# Revit family: Haworth_Planes_HeightAdjustTable_Corner90_WrapAround
name_source: partatom
category: Furniture Systems
revit_build: Autodesk Revit 2018 (Build: 20170223_1515(x64)
units: mm (PartAtom-declared; Revit-internal decimal feet)

## family parameters
Always vertical = Yes
Cut with Voids When Loaded = No
OmniClass Number = 23.40.70.14.64.21
OmniClass Title = Systems Furniture
Part Type = Normal
Room Calculation Point = No
Round Connector Dimension = Use Diameter
Shared = No
Work Plane-Based = No

## types (4) — shared parameters
Actual Height = 40"
Assembly Code = E2020200
Base Tube Finish = Haworth _ Paint _ Smoke
Custom Size = No
Edgeband = Yes
Height = 40"
Knife Edge = No
Leg Inset Length = 6"
Manufacturer = Haworth
Max. Depth = 29"
Max. Height = 46"
Max. Length = 70"
Max. Width = 70"
Min. Depth = 23"
Min. Height = 27"
Min. Length = 46"
Min. Width = 40"
Min/Max Depth = 23 or 29 in.
Min/Max Length = 46-70 in. @ 6 in. increment
Min/Max Width = 40-70 in. @ 6 in. increment
Model = TACR, TACE
Radius = 10 1/4"
Revision Number = 2
Size = Verify Final Dim. w/ Haworth
Support Height = 38 13/16"
Top Thickness = 1 3/16"
URL = www.haworth.com

## per-type parameters (varying)
| type | 23 Deep | Actual Depth | Actual Length | Actual Width | Back Leg Offset | Depth | Description | Length | URL - Product | Warranty | Width |
| 70" x 70" x 29" | No | 29" | 70" | 70" | 9 3/32" | 29" | Haworth Planes - HAT Corner-90 - WrapAround - 70" x 70" x 29" | 70" | https://www.haworth.com | https://www.haworth.com | 70" |
| 52" x 52" x 23" | Yes | 23" | 52" | 52" | 6 3/32" | 23" | Haworth Planes - HAT Corner-90 - WrapAround - 52" x 52" x 23" | 52" | http://www.haworth.com | www.haworth.com/en-us/Products/Pages/Certifications.aspx | 52" |
| 46" x 58" x 23" | Yes | 23" | 58" | 46" | 6 3/32" | 23" | Haworth Planes - HAT Corner-90 - WrapAround - 46" x 58" x 23" | 58" | http://www.haworth.com | www.haworth.com/en-us/Products/Pages/Certifications.aspx | 46" |
| 64" x 70" x 29" | No | 29" | 70" | 64" | 9 3/32" | 29" | Haworth Planes - HAT Corner-90 - WrapAround - 64" x 70" x 29" | 70" | http://www.haworth.com | www.haworth.com/en-us/Products/Pages/Certifications.aspx | 64" |

## geometry (parser evidence)
native form markers: Sweep x8
no freeform markers — native parametric forms only
